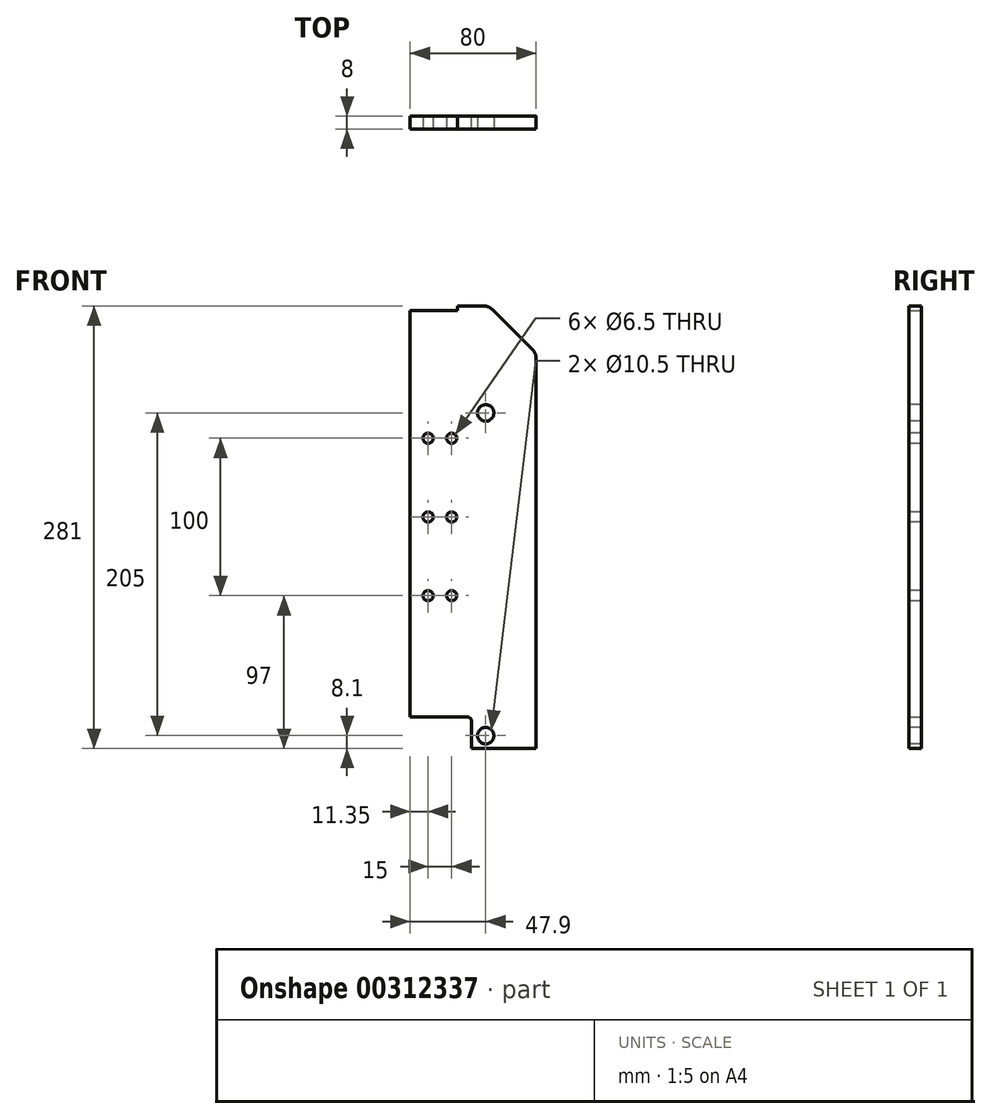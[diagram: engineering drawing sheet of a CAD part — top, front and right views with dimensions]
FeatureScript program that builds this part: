
annotation { "Feature Type Name" : "Feature", "Feature Type Description" : "" }
export const myFeature = defineFeature(function(context is Context, id is Id, definition is map)
    precondition{}
    {
        {
            var Q0;
            Q0=qCreatedBy(makeId("Front.planeOp"),FACE);
            var sketch = newSketch(context, id + "F0", { "sketchPlane" : qUnion([Q0])});
            skLineSegment(sketch, "E0", {"start": v(0, 0) * mm, "end": v(0, 281) * mm});
            skLineSegment(sketch, "E1", {"start": v(0, 281) * mm, "end": v(-50, 281) * mm});
            skLineSegment(sketch, "E2", {"start": v(-50, 281) * mm, "end": v(-50, 278) * mm});
            skLineSegment(sketch, "E3", {"start": v(-50, 278) * mm, "end": v(-80, 278) * mm});
            skLineSegment(sketch, "E4", {"start": v(-80, 278) * mm, "end": v(-80, 20) * mm});
            skLineSegment(sketch, "E5", {"start": v(-80, 20) * mm, "end": v(-41, 20) * mm});
            skLineSegment(sketch, "E6", {"start": v(-41, 20) * mm, "end": v(-41, 0) * mm});
            skLineSegment(sketch, "E7", {"start": v(-41, 0) * mm, "end": v(0, 0) * mm});
            skSolve(sketch);
        }
        {
            var Q0;
            Q0=makeQuery(id+"F0.imprint","IMPRINT",FACE,{"disambiguationData":[TD([[makeQuery(id+"F0.imprint","IMPRINT",EDGE,{"derivedFrom":sQuery(id+"F0.wireOp",EDGE,"E0")}),1.0]])]});
            extrude(context, id + "F1", {"entities" : qUnion([Q0]), "depth" : 8 * mm});
        }
        {
            var Q0;
            Q0=makeQuery(id+"F1.opExtrude","SWEPT_EDGE",EDGE,{"disambiguationData":[OSD([sQuery(id+"F0.wireOp",EDGE,"E0"),sQuery(id+"F0.wireOp",EDGE,"E1")])]});
            chamfer(context, id + "F2", {"entities" : qUnion([Q0]), "width" : 30 * mm, "tangentPropagation" : true});
        }
        {
            var Q0;
            {var subQ0=sQuery(id+"F0.wireOp",EDGE,"E1");Q0=makeQuery(id+"F2.opChamfer","BLEND_EDGE",EDGE,{"blendedFrom":[makeQuery(id+"F1.opExtrude","SWEPT_EDGE",EDGE,{"disambiguationData":[OSD([sQuery(id+"F0.wireOp",EDGE,"E0"),subQ0])]}),makeQuery(id+"F1.opExtrude","SWEPT_FACE",FACE,{"disambiguationData":[OSD([subQ0])]})],"blendedInto":[makeQuery(id+"F1.opExtrude","SWEPT_FACE",FACE,{"disambiguationData":[OSD([subQ0])]})]});}
            var Q1;
            {var subQ0=sQuery(id+"F0.wireOp",EDGE,"E0");Q1=makeQuery(id+"F2.opChamfer","BLEND_EDGE",EDGE,{"blendedFrom":[makeQuery(id+"F1.opExtrude","SWEPT_EDGE",EDGE,{"disambiguationData":[OSD([subQ0,sQuery(id+"F0.wireOp",EDGE,"E1")])]}),makeQuery(id+"F1.opExtrude","SWEPT_FACE",FACE,{"disambiguationData":[OSD([subQ0])]})],"blendedInto":[makeQuery(id+"F1.opExtrude","SWEPT_FACE",FACE,{"disambiguationData":[OSD([subQ0])]})]});}
            fillet(context, id + "F3", {"entities" : qUnion([Q0, Q1]), "radius" : 8 * mm, "tangentPropagation" : true, "allowEdgeOverflow" : false});
        }
        {
            var Q0;
            Q0=makeQuery(id+"F1.opExtrude","SWEPT_EDGE",EDGE,{"disambiguationData":[OSD([sQuery(id+"F0.wireOp",EDGE,"E5"),sQuery(id+"F0.wireOp",EDGE,"E6")])]});
            fillet(context, id + "F4", {"entities" : qUnion([Q0]), "radius" : 3 * mm, "tangentPropagation" : true, "allowEdgeOverflow" : false});
        }
        {
            var Q0;
            Q0=makeQuery(id+"F1.opExtrude","CAP_FACE",FACE,{"disambiguationData":[OSD([sQuery(id+"F0.wireOp",EDGE,"E0"),sQuery(id+"F0.wireOp",EDGE,"E1"),sQuery(id+"F0.wireOp",EDGE,"E2"),sQuery(id+"F0.wireOp",EDGE,"E3"),sQuery(id+"F0.wireOp",EDGE,"E4"),sQuery(id+"F0.wireOp",EDGE,"E5"),sQuery(id+"F0.wireOp",EDGE,"E6"),sQuery(id+"F0.wireOp",EDGE,"E7")])],"isStart":false});
            var sketch = newSketch(context, id + "F5", { "sketchPlane" : qUnion([Q0])});
            skLineSegment(sketch, "E8.bottom", {"start": v(-53.65, 97) * mm, "end": v(-68.65, 97) * mm, "construction": true});
            skLineSegment(sketch, "E8.top", {"start": v(-53.65, 197) * mm, "end": v(-68.65, 197) * mm, "construction": true});
            skLineSegment(sketch, "E8.left", {"start": v(-53.65, 97) * mm, "end": v(-53.65, 197) * mm, "construction": true});
            skLineSegment(sketch, "E8.right", {"start": v(-68.65, 97) * mm, "end": v(-68.65, 197) * mm, "construction": true});
            skPoint(sketch, "E8.middle", {"position": v(-61.15, 147) * mm});
            skLineSegment(sketch, "E9", {"start": v(-68.65, 147) * mm, "end": v(-53.65, 147) * mm, "construction": true});
            skSolve(sketch);
        }
        {
            var Q0;
            Q0=sQuery(id+"F5.wireOp",VERTEX,"E8.top.end");
            var Q1;
            Q1=sQuery(id+"F5.wireOp",VERTEX,"E8.left.end");
            var Q2;
            Q2=sQuery(id+"F5.wireOp",VERTEX,"E9.end");
            var Q3;
            Q3=sQuery(id+"F5.wireOp",VERTEX,"E9.start");
            var Q4;
            Q4=sQuery(id+"F5.wireOp",VERTEX,"E8.left.start");
            var Q5;
            Q5=sQuery(id+"F5.wireOp",VERTEX,"E8.right.start");
            var Q6;
            Q6=makeQuery(id+"F1.opExtrude","SWEPT_BODY",BODY,{"disambiguationData":[OSD([sQuery(id+"F0.wireOp",EDGE,"E0"),sQuery(id+"F0.wireOp",EDGE,"E1"),sQuery(id+"F0.wireOp",EDGE,"E2"),sQuery(id+"F0.wireOp",EDGE,"E3"),sQuery(id+"F0.wireOp",EDGE,"E4"),sQuery(id+"F0.wireOp",EDGE,"E5"),sQuery(id+"F0.wireOp",EDGE,"E6"),sQuery(id+"F0.wireOp",EDGE,"E7")])]});
            hole(context, id + "F6", {"style" : HoleStyle.SIMPLE, "endStyle" : HoleEndStyle.THROUGH, "holeDiameter" : 6.5 * mm, "tappedDepth" : 12 * mm, "tapClearance" : 3, "locations" : qUnion([Q0, Q1, Q2, Q3, Q4, Q5]), "scope" : qUnion([Q6])});
        }
        {
            var Q0;
            Q0=makeQuery(id+"F1.opExtrude","CAP_FACE",FACE,{"disambiguationData":[OSD([sQuery(id+"F0.wireOp",EDGE,"E0"),sQuery(id+"F0.wireOp",EDGE,"E1"),sQuery(id+"F0.wireOp",EDGE,"E2"),sQuery(id+"F0.wireOp",EDGE,"E3"),sQuery(id+"F0.wireOp",EDGE,"E4"),sQuery(id+"F0.wireOp",EDGE,"E5"),sQuery(id+"F0.wireOp",EDGE,"E6"),sQuery(id+"F0.wireOp",EDGE,"E7")])],"isStart":false});
            var sketch = newSketch(context, id + "F7", { "sketchPlane" : qUnion([Q0])});
            skLineSegment(sketch, "E10", {"start": v(-32.1, 213.1) * mm, "end": v(-32.1, 8.1) * mm, "construction": true});
            skSolve(sketch);
        }
        {
            var Q0;
            Q0=sQuery(id+"F7.wireOp",VERTEX,"E10.start");
            var Q1;
            Q1=sQuery(id+"F7.wireOp",VERTEX,"E10.end");
            var Q2;
            Q2=makeQuery(id+"F1.opExtrude","SWEPT_BODY",BODY,{"disambiguationData":[OSD([sQuery(id+"F0.wireOp",EDGE,"E0"),sQuery(id+"F0.wireOp",EDGE,"E1"),sQuery(id+"F0.wireOp",EDGE,"E2"),sQuery(id+"F0.wireOp",EDGE,"E3"),sQuery(id+"F0.wireOp",EDGE,"E4"),sQuery(id+"F0.wireOp",EDGE,"E5"),sQuery(id+"F0.wireOp",EDGE,"E6"),sQuery(id+"F0.wireOp",EDGE,"E7")])]});
            hole(context, id + "F8", {"style" : HoleStyle.SIMPLE, "endStyle" : HoleEndStyle.THROUGH, "holeDiameter" : 10.5 * mm, "tappedDepth" : 12 * mm, "tapClearance" : 3, "locations" : qUnion([Q0, Q1]), "scope" : qUnion([Q2])});
        }
    });
